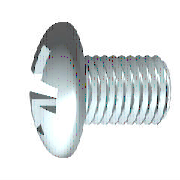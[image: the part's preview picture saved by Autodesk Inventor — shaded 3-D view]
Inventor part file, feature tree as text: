
AUTODESK INVENTOR PART (.ipt)
format: ipt  version: 2019 (Build 230136000, 136)  size: 275,456 bytes
history: native  units: mm (DEFAULTED — no unit token found)
features: other x2, plane x2, extrude x1
ambient origin geometry x7: Origin, YZ Plane, XZ Plane, X Axis, Y Axis, Z Axis, Center Point
bodies: Solid1 (feature_tree)
feature tree (5):
  other  "Cuerpo"
  plane  "Work Plane1"
  extrude  "Ranura"  Depth=4.0mm
  other  "Corte"
  plane  "Work Plane3"
